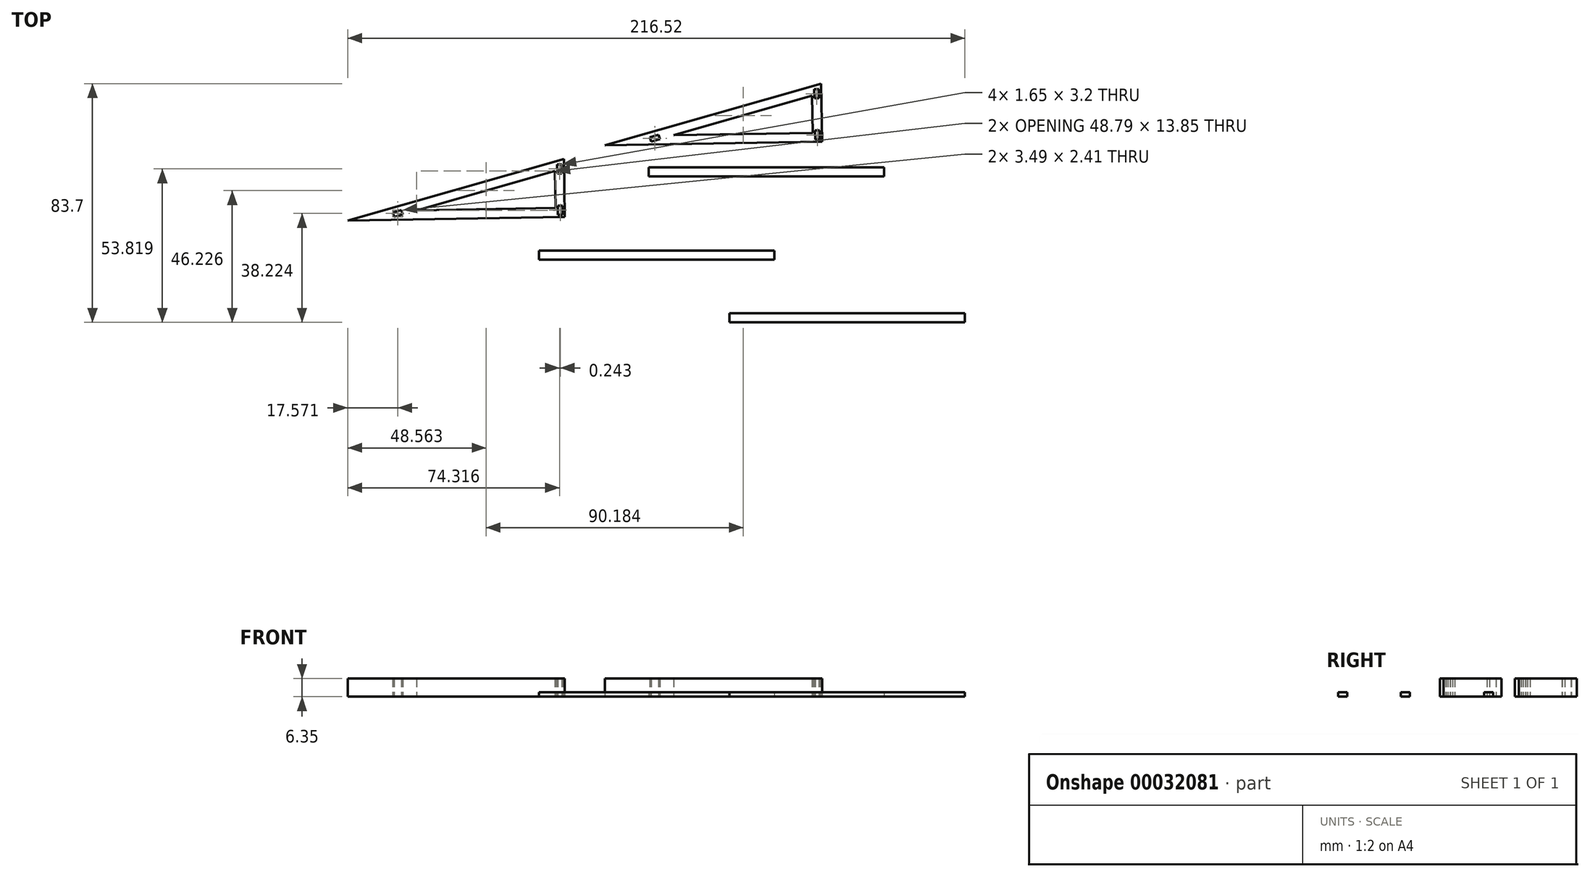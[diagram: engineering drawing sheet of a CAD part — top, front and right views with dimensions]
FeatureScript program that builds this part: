
annotation { "Feature Type Name" : "Feature", "Feature Type Description" : "" }
export const myFeature = defineFeature(function(context is Context, id is Id, definition is map)
    precondition{}
    {
        {
            var Q0;
            Q0=qCreatedBy(makeId("Top.planeOp"),FACE);
            var sketch = newSketch(context, id + "F0", { "sketchPlane" : qUnion([Q0])});
            skLineSegment(sketch, "E0", {"start": v(39.3, 18.81) * mm, "end": v(115.5, 20.13) * mm});
            skLineSegment(sketch, "E1", {"start": v(115.5, 20.13) * mm, "end": v(115.14, 40.45) * mm});
            skLineSegment(sketch, "E2", {"start": v(39.3, 18.81) * mm, "end": v(115.14, 40.45) * mm});
            skLineSegment(sketch, "E3", {"start": v(50.85, 22.19) * mm, "end": v(51.15, 22.2) * mm});
            skLineSegment(sketch, "E4", {"start": v(112.26, 23.25) * mm, "end": v(112.04, 36.26) * mm});
            skLineSegment(sketch, "E5", {"start": v(112.04, 36.26) * mm, "end": v(63.47, 22.4) * mm});
            skLineSegment(sketch, "E6.trimOffspring", {"start": v(63.47, 22.4) * mm, "end": v(112.26, 23.25) * mm});
            skLineSegment(sketch, "E7", {"start": v(112.8, 38.5) * mm, "end": v(112.85, 35.32) * mm});
            skLineSegment(sketch, "E8", {"start": v(112.85, 35.32) * mm, "end": v(114.45, 35.35) * mm});
            skLineSegment(sketch, "E9", {"start": v(114.45, 35.35) * mm, "end": v(114.4, 38.53) * mm});
            skLineSegment(sketch, "E10", {"start": v(114.4, 38.53) * mm, "end": v(112.8, 38.5) * mm});
            skLineSegment(sketch, "E11", {"start": v(113.1, 20.87) * mm, "end": v(114.7, 20.9) * mm});
            skLineSegment(sketch, "E12", {"start": v(113.04, 24.05) * mm, "end": v(113.1, 20.87) * mm});
            skLineSegment(sketch, "E13", {"start": v(114.64, 24.08) * mm, "end": v(113.04, 24.05) * mm});
            skLineSegment(sketch, "E14", {"start": v(114.7, 20.9) * mm, "end": v(114.64, 24.08) * mm});
            skLineSegment(sketch, "E15", {"start": v(55.13, 21.66) * mm, "end": v(55.57, 20.13) * mm});
            skLineSegment(sketch, "E16", {"start": v(58.18, 22.54) * mm, "end": v(55.13, 21.66) * mm});
            skLineSegment(sketch, "E17", {"start": v(58.62, 21) * mm, "end": v(58.18, 22.54) * mm});
            skLineSegment(sketch, "E18", {"start": v(55.57, 20.13) * mm, "end": v(58.62, 21) * mm});
            skLineSegment(sketch, "E19", {"start": v(63.47, 22.4) * mm, "end": v(51.62, 19.03) * mm, "construction": true});
            skSolve(sketch);
        }
        {
            var Q0;
            {var subQ3=sQuery(id+"F0.wireOp",EDGE,"E0");Q0=makeQuery(id+"F0.imprint","IMPRINT",FACE,{"disambiguationData":[TD([[makeQuery(id+"F0.imprint","IMPRINT",EDGE,{"derivedFrom":subQ3}),1.0]])]});}
            extrude(context, id + "F1", {"entities" : qUnion([Q0]), "depth" : 6.35 * mm});
        }
        {
            var Q0;
            Q0=qCreatedBy(makeId("Top.planeOp"),FACE);
            var sketch = newSketch(context, id + "F2", { "sketchPlane" : qUnion([Q0])});
            skLineSegment(sketch, "E20", {"start": v(-50.88, -7.54) * mm, "end": v(25.3, -6.23) * mm});
            skLineSegment(sketch, "E21", {"start": v(25.3, -6.23) * mm, "end": v(24.96, 14.09) * mm});
            skLineSegment(sketch, "E22", {"start": v(-50.88, -7.54) * mm, "end": v(24.96, 14.09) * mm});
            skLineSegment(sketch, "E23", {"start": v(-39.34, -4.17) * mm, "end": v(-39.03, -4.16) * mm});
            skLineSegment(sketch, "E24", {"start": v(22.08, -3.1) * mm, "end": v(21.85, 9.9) * mm});
            skLineSegment(sketch, "E25", {"start": v(21.85, 9.9) * mm, "end": v(-26.71, -3.95) * mm});
            skLineSegment(sketch, "E26.trimOffspring", {"start": v(-26.71, -3.95) * mm, "end": v(22.08, -3.1) * mm});
            skLineSegment(sketch, "E27", {"start": v(22.6, 12.14) * mm, "end": v(22.66, 8.97) * mm});
            skLineSegment(sketch, "E28", {"start": v(22.66, 8.97) * mm, "end": v(24.26, 9) * mm});
            skLineSegment(sketch, "E29", {"start": v(24.26, 9) * mm, "end": v(24.2, 12.17) * mm});
            skLineSegment(sketch, "E30", {"start": v(24.2, 12.17) * mm, "end": v(22.6, 12.14) * mm});
            skLineSegment(sketch, "E31", {"start": v(22.9, -5.48) * mm, "end": v(24.5, -5.46) * mm});
            skLineSegment(sketch, "E32", {"start": v(22.85, -2.3) * mm, "end": v(22.9, -5.48) * mm});
            skLineSegment(sketch, "E33", {"start": v(24.45, -2.28) * mm, "end": v(22.85, -2.3) * mm});
            skLineSegment(sketch, "E34", {"start": v(24.5, -5.46) * mm, "end": v(24.45, -2.28) * mm});
            skLineSegment(sketch, "E35", {"start": v(-35.05, -4.7) * mm, "end": v(-34.62, -6.23) * mm});
            skLineSegment(sketch, "E36", {"start": v(-32, -3.82) * mm, "end": v(-35.05, -4.7) * mm});
            skLineSegment(sketch, "E37", {"start": v(-31.56, -5.36) * mm, "end": v(-32, -3.82) * mm});
            skLineSegment(sketch, "E38", {"start": v(-34.62, -6.23) * mm, "end": v(-31.56, -5.36) * mm});
            skLineSegment(sketch, "E39", {"start": v(-26.71, -3.95) * mm, "end": v(-38.56, -7.33) * mm, "construction": true});
            skSolve(sketch);
        }
        {
            var Q0;
            Q0 = qSketchRegion(id + "F2", true);
            extrude(context, id + "F3", {"entities" : qUnion([Q0]), "depth" : 6.35 * mm});
        }
        {
            var Q0;
            Q0=qCreatedBy(makeId("Top.planeOp"),FACE);
            var sketch = newSketch(context, id + "F4", { "sketchPlane" : qUnion([Q0])});
            skLineSegment(sketch, "E40.bottom", {"start": v(54.7, 11.18) * mm, "end": v(137.25, 11.18) * mm});
            skLineSegment(sketch, "E40.top", {"start": v(54.7, 8) * mm, "end": v(137.25, 8) * mm});
            skLineSegment(sketch, "E40.left", {"start": v(54.7, 11.18) * mm, "end": v(54.7, 8) * mm});
            skLineSegment(sketch, "E40.right", {"start": v(137.25, 11.18) * mm, "end": v(137.25, 8) * mm});
            skLineSegment(sketch, "E41.top", {"start": v(16.25, -21.26) * mm, "end": v(98.8, -21.26) * mm});
            skLineSegment(sketch, "E41.bottom", {"start": v(16.25, -18.09) * mm, "end": v(98.8, -18.09) * mm});
            skLineSegment(sketch, "E41.right", {"start": v(98.8, -18.09) * mm, "end": v(98.8, -21.26) * mm});
            skLineSegment(sketch, "E41.left", {"start": v(16.25, -18.09) * mm, "end": v(16.25, -21.26) * mm});
            skLineSegment(sketch, "E42.top", {"start": v(83.1, -43.25) * mm, "end": v(165.64, -43.25) * mm});
            skLineSegment(sketch, "E42.bottom", {"start": v(83.1, -40.08) * mm, "end": v(165.64, -40.08) * mm});
            skLineSegment(sketch, "E42.right", {"start": v(165.64, -40.08) * mm, "end": v(165.64, -43.25) * mm});
            skLineSegment(sketch, "E42.left", {"start": v(83.1, -40.08) * mm, "end": v(83.1, -43.25) * mm});
            skSolve(sketch);
        }
        {
            var Q0;
            Q0 = qSketchRegion(id + "F4", true);
            extrude(context, id + "F5", {"entities" : qUnion([Q0]), "depth" : 1.6 * mm});
        }
    });
